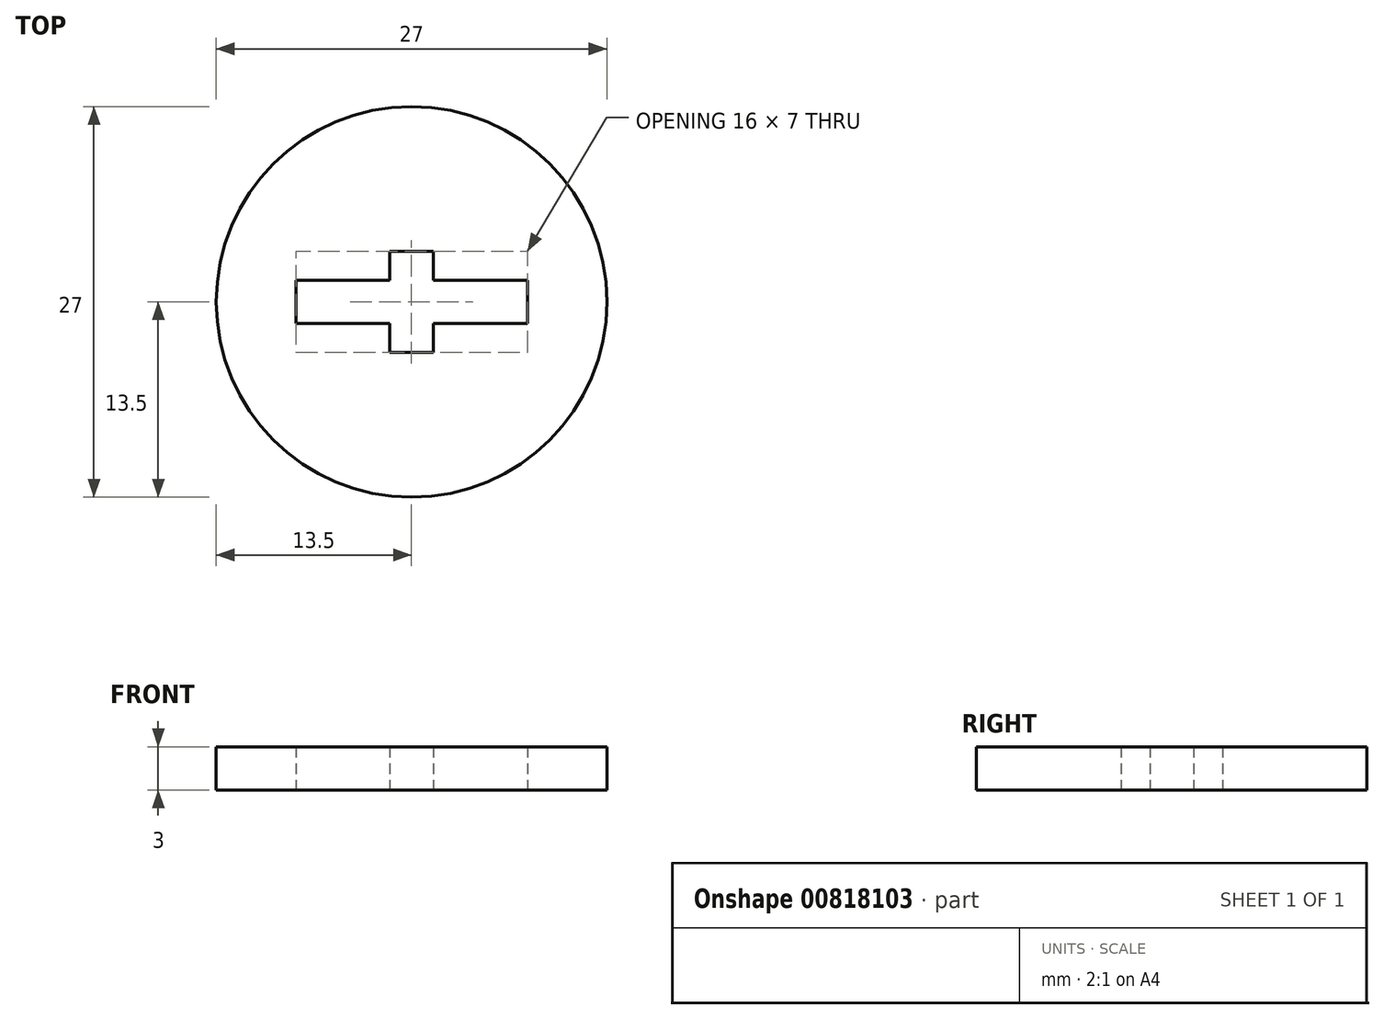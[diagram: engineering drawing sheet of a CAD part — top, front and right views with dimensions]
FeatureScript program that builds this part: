
annotation { "Feature Type Name" : "Feature", "Feature Type Description" : "" }
export const myFeature = defineFeature(function(context is Context, id is Id, definition is map)
    precondition{}
    {
        {
            var Q0;
            Q0=qCreatedBy(makeId("Top.planeOp"),FACE);
            var sketch = newSketch(context, id + "F0", { "sketchPlane" : qUnion([Q0])});
            skLineSegment(sketch, "E0", {"start": v(-1.5, 3.5) * mm, "end": v(-1.5, 1.5) * mm});
            skLineSegment(sketch, "E1", {"start": v(-1.5, 1.5) * mm, "end": v(-8, 1.5) * mm});
            skLineSegment(sketch, "E2", {"start": v(-8, 1.5) * mm, "end": v(-8, -1.5) * mm});
            skLineSegment(sketch, "E3", {"start": v(-8, -1.5) * mm, "end": v(-1.5, -1.5) * mm});
            skLineSegment(sketch, "E4", {"start": v(-1.5, -1.5) * mm, "end": v(-1.5, -3.5) * mm});
            skLineSegment(sketch, "E5.MirrorCS", {"start": v(1.5, 3.5) * mm, "end": v(1.5, 1.5) * mm});
            skLineSegment(sketch, "E6.MirrorCS", {"start": v(1.5, 1.5) * mm, "end": v(8, 1.5) * mm});
            skLineSegment(sketch, "E7.MirrorCS", {"start": v(8, 1.5) * mm, "end": v(8, -1.5) * mm});
            skLineSegment(sketch, "E8.MirrorCS", {"start": v(8, -1.5) * mm, "end": v(1.5, -1.5) * mm});
            skLineSegment(sketch, "E9.MirrorCS", {"start": v(1.5, -1.5) * mm, "end": v(1.5, -3.5) * mm});
            skPoint(sketch, "E10.middle", {"position": v(0, 0) * mm});
            skLineSegment(sketch, "E11", {"start": v(-1.5, 3.5) * mm, "end": v(1.5, 3.5) * mm});
            skLineSegment(sketch, "E12", {"start": v(-1.5, -3.5) * mm, "end": v(1.5, -3.5) * mm});
            skCircle(sketch, "E13", {"center": v(0, 0) * mm, "radius": 13.5 * mm});
            skSolve(sketch);
        }
        {
            var Q0;
            Q0 = qSketchRegion(id + "F0", true);
            extrude(context, id + "F1", {"entities" : qUnion([Q0]), "depth" : 3 * mm, "offsetDistance" : 25 * mm});
        }
    });
